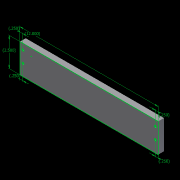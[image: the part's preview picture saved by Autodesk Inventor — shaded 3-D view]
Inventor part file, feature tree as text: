
AUTODESK INVENTOR PART (.ipt)
format: ipt  version: 2012 (Build 160160000, 160)  size: 98,816 bytes
history: native  units: in
note: dims shown in document units (in); Inventor stores cm internally (conversion verified against a paired STEP export)
features: hole x4, sketch x3, extrude x1
ambient origin geometry x8: Origin, YZ Plane, XZ Plane, XY Plane, X Axis, Y Axis, Z Axis, Center Point
bodies: Solid1 (feature_tree)
feature tree (8):
  extrude  "Extrusion1"  Depth=2.5in
  hole  "Hole1"  [1 undecoded]
  hole  "Hole2"  [1 undecoded]
  hole  "Hole3"  [1 undecoded]
  hole  "Hole4"  [1 undecoded]
  sketch  "Sketch2"  dims[d2=0.5in d3=0.0in d4=0.5in d5=0.25in]
  sketch  "Sketch3"  dims[d6=0.19in d7=0.75in d8=0.375in d9=0.25in d10=0.5635in d11=1.0in d12=0.8108in d13=0.25in d14=1.0in d15=0.19in d16=0.75in d17=0.375in d18=0.25in d19=0.5635in d20=1.0in d21=0.8108in d22=0.5in d23=0.25in d24=0.19in d25=0.75in d26=0.375in d27=0.25in d28=0.5635in d29=1.0in d30=0.8108in d31=1.5in d32=0.25in d33=0.19in d34=0.75in d35=0.375in d36=0.25in d37=0.5635in d38=1.0in d39=0.8108in d40=12.0in d41=2.5in d42=0.25in d43=0.25in d44=0.25in d45=0.25in]
  sketch  "Sketch1"  dims[d0=12.0in d1=2.5in]
note: 4 required parameter values undecoded (feature->parameter linkage not recoverable at this tier; creation-order binding heuristic only, values carry confidence <= 0.55)
